# Revit family: Domotics-DomesticRanges-GEWISS-CHORUS_COMMAND-BADGE_SWITCH_2M
name_source: partatom
category: Apparecchi elettrici
revit_build: Autodesk Revit 2016 (Build: 20161004_0715(x64)
units: mm (PartAtom-declared; Revit-internal decimal feet)

## family parameters
Condiviso = Sì
Host = Superficie
Mantenere orientamento annotazione = Sì
Numero OmniClass = 23.80.50.11.14
Punto di calcolo locali = Sì
Quota connettore circolare = Usa diametro
Taglio con vuoti quando caricato = Sì
Tipo di parte = Normale
Titolo OmniClass = Switches

## types (3) — shared parameters
Breaking capacity: = 1.25 In (200 position changes)
Carico apparente = 0 VA
Catalogue = DOMOTICS
Catalogue Range = CHORUS - DOMESTIC RANGE
Category = Badge switch
Description: = 1P NA - 16 AX illuminable
Electrocod = 0134
For badge card max. width = 54MM
Glow Wire Test = 850°C
IDF = 80e14bcf-06a4-4b7a-9d78-4e2b63c1345c
IDT = f4165ae2-ed93-4e05-9768-6653f7821cea
Immagine tipo = GW14039.jpg
Insulation resistance = > 5 MOhm
Larghezza pulsante = 46 mm  [stored 0.150919 ft]
N poli = 1
No. Chorus modules = 2
Produttore = GEWISS S.p.A.
Prolonged operation (no.of position changes) = 40.000 at In 250 V ac cosÃ˜=0,6
Prospetto di default = 1219 mm
Resistance at test voltage = 2000 V at 50 Hz for 1 minute
SEO = Badge switch
Standard; = EN 60669-1
Technical sheet = https://www.gewiss.com
Terminal grip on cable traction = > 50 N
Terminal tightening capacity flexible cables (mm2) = min. 0,75 - max. 2x4
Terminal tightening capacity rigid cables (mm2) = min. 0,5 - max. 2x2,5
Thermo-pressure with ball = 125
Tipo_ = BADGE 2M : GW14039 Badge elettromeccanico 2M titanio
Type = Illuminable
URL = https://www.gewiss.com
Version file RFA = 19.0
Volt = 230 V
Wiring terminals = With screw

## per-type parameters (varying)
| type | Colour | Descrizione | EAN code | Modello |
| GW10039 - Badge switch 1P 2M white | White | BADGE SWITCH 1P 2M CH/WT | 8011564439306 | GW10039 |
| GW14039 - Badge-operated mech.switch 2M titanium | Titanium | BADGE-OPERATED MECH.SWITCH 2M TITANIUM | 8011564439320 | GW14039 |
| GW12039 - Badge-operated mech.switch 2M black | Black | BADGE-OPERATED MECH.SWITCH 2M BLACK | 8011564439313 | GW12039 |

note: source unit labels omitted for Thermo-pressure with ball — the stored unit's dimension contradicts the parameter name (converter mislabeling)

note: [stored X ft] marks values corroborated as IEEE doubles in the binary element streams (Revit-internal decimal feet)

## geometry (parser evidence)
native form markers: Sweep x1
no freeform markers — native parametric forms only
